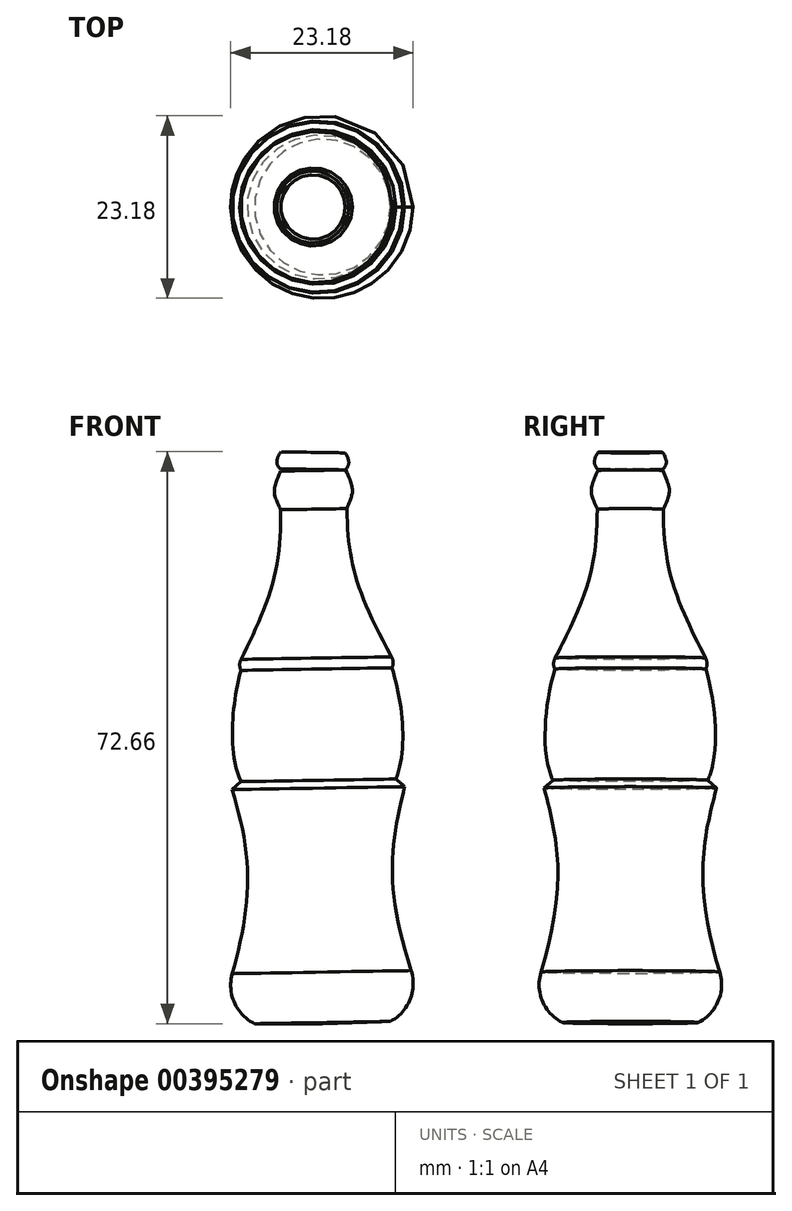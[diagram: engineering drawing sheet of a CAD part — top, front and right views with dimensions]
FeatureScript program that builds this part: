
annotation { "Feature Type Name" : "Feature", "Feature Type Description" : "" }
export const myFeature = defineFeature(function(context is Context, id is Id, definition is map)
    precondition{}
    {
        {
            var Q0;
            Q0=qCreatedBy(makeId("Front.planeOp"),FACE);
            var sketch = newSketch(context, id + "F0", { "sketchPlane" : qUnion([Q0])});
            skFitSpline(sketch, "E0", {"points": [v(-32.02, 18.24) * mm, v(-37.06, -0.77) * mm], "startDerivative": vector(0.32, -20.8) * mm, "endDerivative": vector(-12.64, -25.36) * mm});
            skLineSegment(sketch, "E1", {"start": v(-32.02, 18.24) * mm, "end": v(-27.82, 18.24) * mm});
            skFitSpline(sketch, "E2", {"points": [v(-32.02, 18.24) * mm, v(-32.02, 23.16) * mm], "startDerivative": vector(-2.65, 6.35) * mm, "endDerivative": vector(3.66, 8.4) * mm});
            skLineSegment(sketch, "E3", {"start": v(-32.02, 23.16) * mm, "end": v(-27.9, 23.16) * mm});
            skArc(sketch, "E4", {"start": v(-37.06, -0.77) * mm, "mid": v(-37.23, -1.46) * mm, "end": v(-37.06, -2.16) * mm});
            skFitSpline(sketch, "E5", {"points": [v(-37.06, -2.16) * mm, v(-37.06, -16.3) * mm], "startDerivative": vector(-3.66, -13.72) * mm, "endDerivative": vector(5.06, -10.95) * mm});
            skLineSegment(sketch, "E6", {"start": v(-37.06, -16.3) * mm, "end": v(-38.16, -17.31) * mm});
            skFitSpline(sketch, "E7", {"points": [v(-38.16, -17.31) * mm, v(-38.16, -40.7) * mm], "startDerivative": vector(6.44, -22.2) * mm, "endDerivative": vector(-9.02, -31.7) * mm});
            skArc(sketch, "E8", {"start": v(-38.16, -40.7) * mm, "mid": v(-37.9, -44.38) * mm, "end": v(-35.33, -47.05) * mm});
            skLineSegment(sketch, "E9", {"start": v(-35.33, -47.05) * mm, "end": v(-26.7, -47.05) * mm});
            skLineSegment(sketch, "E10", {"start": v(-27.9, 23.16) * mm, "end": v(-26.7, -47.05) * mm});
            skPoint(sketch, "E10.startSnap0", {"position": v(-27.94, 18.24) * mm});
            skPoint(sketch, "E11.orphan", {"position": v(-18.06, -47.05) * mm});
            skSolve(sketch);
        }
        {
            var Q0;
            Q0=makeQuery(id+"F0.imprint","IMPRINT",FACE,{"disambiguationData":[TD([[makeQuery(id+"F0.imprint","IMPRINT",EDGE,{"derivedFrom":sQuery(id+"F0.wireOp",EDGE,"E0")}),1.0]])]});
            var Q1;
            {var subQ0=sQuery(id+"F0.wireOp",EDGE,"E1");Q1=makeQuery(id+"F0.imprint","IMPRINT",FACE,{"disambiguationData":[TD([[makeQuery(id+"F0.imprint","IMPRINT",EDGE,{"derivedFrom":subQ0}),1.0]])]});}
            var Q2;
            {var subQ0=sQuery(id+"F0.wireOp",EDGE,"E3");Q2=makeQuery(id+"F0.imprint","IMPRINT",FACE,{"disambiguationData":[TD([[makeQuery(id+"F0.imprint","IMPRINT",EDGE,{"derivedFrom":subQ0}),1.0]])]});}
            var Q3;
            Q3=sQuery(id+"F0.wireOp",EDGE,"E10");
            revolve(context, id + "F1", {"entities" : qUnion([Q0, Q1, Q2]), "axis" : qUnion([Q3]), "revolveType" : RevolveType.FULL});
        }
        {
            var Q0;
            Q0=makeQuery(id+"F1.opRevolve","SWEPT_EDGE",EDGE,{"disambiguationData":[OSD([sQuery(id+"F0.wireOp",EDGE,"E2"),sQuery(id+"F0.wireOp",EDGE,"E3")])]});
            cPlane(context, id + "F2", {"entities" : qUnion([Q0]), "cplaneType" : CPlaneType.LINE_ANGLE, "offset" : 25.4 * mm, "angle" : 90 * degree, "width" : 152.4 * mm, "height" : 152.4 * mm});
        }
        {
            var Q0;
            Q0=qCreatedBy(id+"F2.planeOp",FACE);
            var sketch = newSketch(context, id + "F3", { "sketchPlane" : qUnion([Q0])});
            skLineSegment(sketch, "E12", {"start": v(23.83, 23.3) * mm, "end": v(27.95, 23.3) * mm});
            skFitSpline(sketch, "E13", {"points": [v(23.83, 23.3) * mm, v(23.83, 25.47) * mm], "startDerivative": vector(-1.47, 1.47) * mm, "endDerivative": vector(2.2, 3.39) * mm});
            skLineSegment(sketch, "E14", {"start": v(23.83, 25.47) * mm, "end": v(27.91, 25.47) * mm});
            skLineSegment(sketch, "E15", {"start": v(27.91, 25.47) * mm, "end": v(27.95, 23.3) * mm});
            skSolve(sketch);
        }
        {
            var Q0;
            Q0=makeQuery(id+"F3.imprint","IMPRINT",FACE,{"disambiguationData":[TD([[makeQuery(id+"F3.imprint","IMPRINT",EDGE,{"derivedFrom":sQuery(id+"F3.wireOp",EDGE,"E12")}),1.0]])]});
            var Q1;
            Q1=sQuery(id+"F3.wireOp",EDGE,"E15");
            revolve(context, id + "F4", {"entities" : qUnion([Q0]), "axis" : qUnion([Q1]), "revolveType" : RevolveType.FULL});
        }
    });
